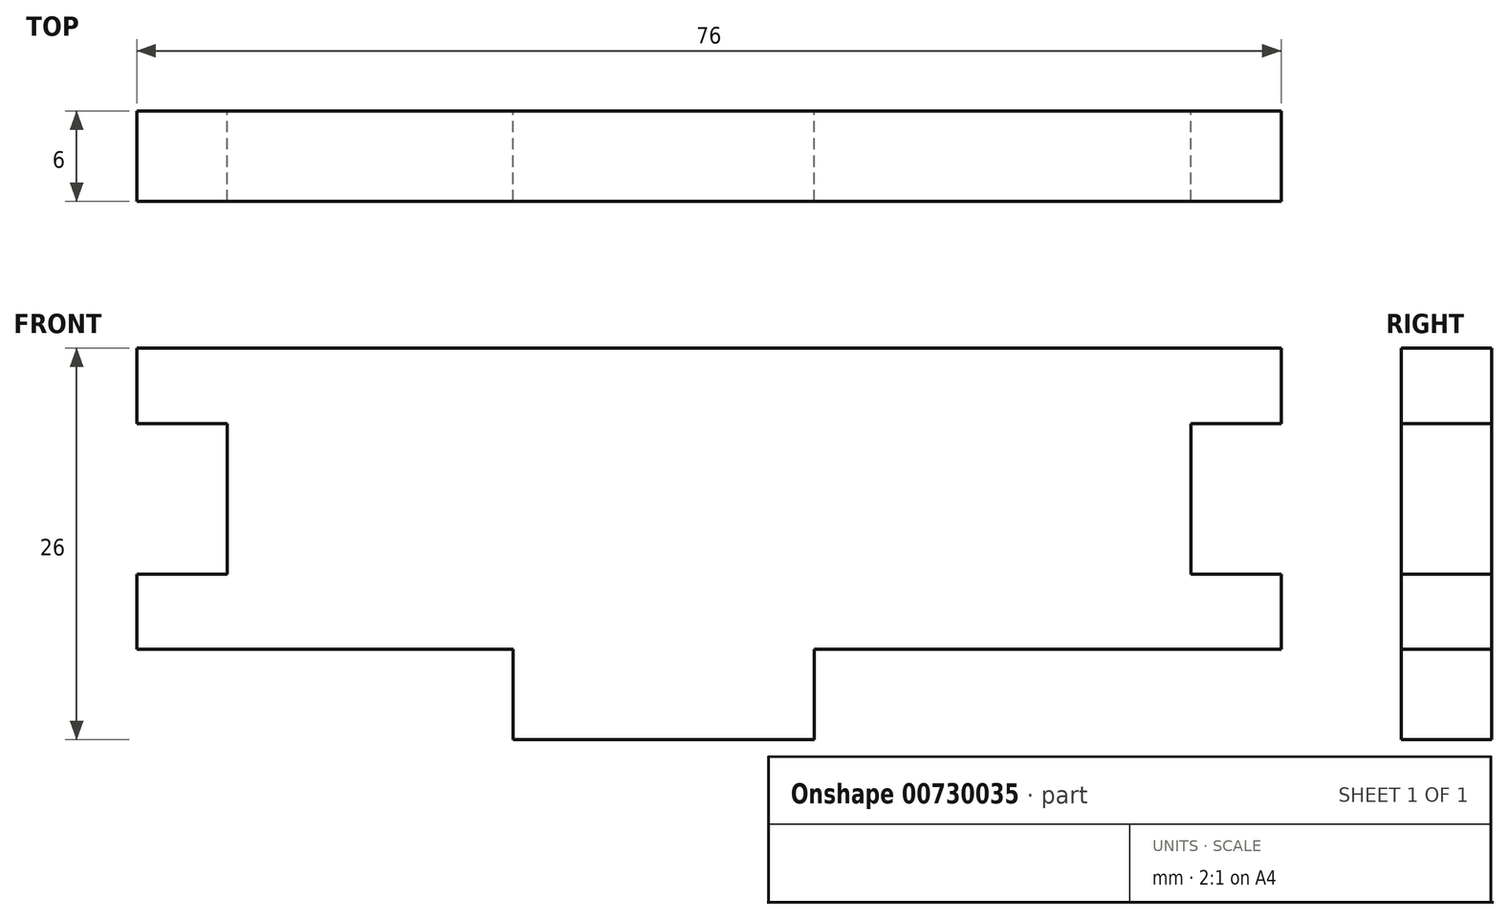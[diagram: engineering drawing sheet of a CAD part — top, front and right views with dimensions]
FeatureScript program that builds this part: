
annotation { "Feature Type Name" : "Feature", "Feature Type Description" : "" }
export const myFeature = defineFeature(function(context is Context, id is Id, definition is map)
    precondition{}
    {
        {
            var Q0;
            Q0=qCreatedBy(makeId("Front.planeOp"),FACE);
            var sketch = newSketch(context, id + "F0", { "sketchPlane" : qUnion([Q0])});
            skLineSegment(sketch, "E0.MirrorCS", {"start": v(-36.28, 15.67) * mm, "end": v(-36.28, 9.67) * mm});
            skLineSegment(sketch, "E1.MirrorCS", {"start": v(8.72, 20.67) * mm, "end": v(8.72, 30.67) * mm});
            skLineSegment(sketch, "E2.MirrorCS", {"start": v(-61.28, 15.67) * mm, "end": v(-36.28, 15.67) * mm});
            skLineSegment(sketch, "E3.MirrorCS", {"start": v(-16.28, 9.67) * mm, "end": v(-16.28, 15.67) * mm});
            skLineSegment(sketch, "E4.MirrorCS", {"start": v(14.72, 30.67) * mm, "end": v(14.72, 35.67) * mm});
            skLineSegment(sketch, "E5.MirrorCS", {"start": v(14.72, 15.67) * mm, "end": v(14.72, 20.67) * mm});
            skLineSegment(sketch, "E6.MirrorCS", {"start": v(-36.28, 9.67) * mm, "end": v(-16.28, 9.67) * mm});
            skLineSegment(sketch, "E7.MirrorCS", {"start": v(8.72, 30.67) * mm, "end": v(14.72, 30.67) * mm});
            skLineSegment(sketch, "E8.MirrorCS", {"start": v(-16.28, 15.67) * mm, "end": v(14.72, 15.67) * mm});
            skLineSegment(sketch, "E9.MirrorCS", {"start": v(-61.28, 35.67) * mm, "end": v(14.72, 35.67) * mm});
            skLineSegment(sketch, "E10.MirrorCS", {"start": v(14.72, 20.67) * mm, "end": v(8.72, 20.67) * mm});
            skLineSegment(sketch, "E11", {"start": v(-61.28, 15.67) * mm, "end": v(-61.28, 20.67) * mm});
            skLineSegment(sketch, "E12", {"start": v(-61.28, 20.67) * mm, "end": v(-55.28, 20.67) * mm});
            skLineSegment(sketch, "E13", {"start": v(-55.28, 20.67) * mm, "end": v(-55.28, 30.67) * mm});
            skLineSegment(sketch, "E14", {"start": v(-55.28, 30.67) * mm, "end": v(-61.28, 30.67) * mm});
            skLineSegment(sketch, "E15", {"start": v(-61.28, 30.67) * mm, "end": v(-61.28, 35.67) * mm});
            skSolve(sketch);
        }
        {
            var Q0;
            Q0=makeQuery(id+"F0.imprint","IMPRINT",FACE,{"disambiguationData":[TD([[makeQuery(id+"F0.imprint","IMPRINT",EDGE,{"derivedFrom":sQuery(id+"F0.wireOp",EDGE,"E0.MirrorCS")}),1.0]])]});
            extrude(context, id + "F1", {"entities" : qUnion([Q0]), "depth" : 6 * mm, "offsetDistance" : 25 * mm});
        }
    });
